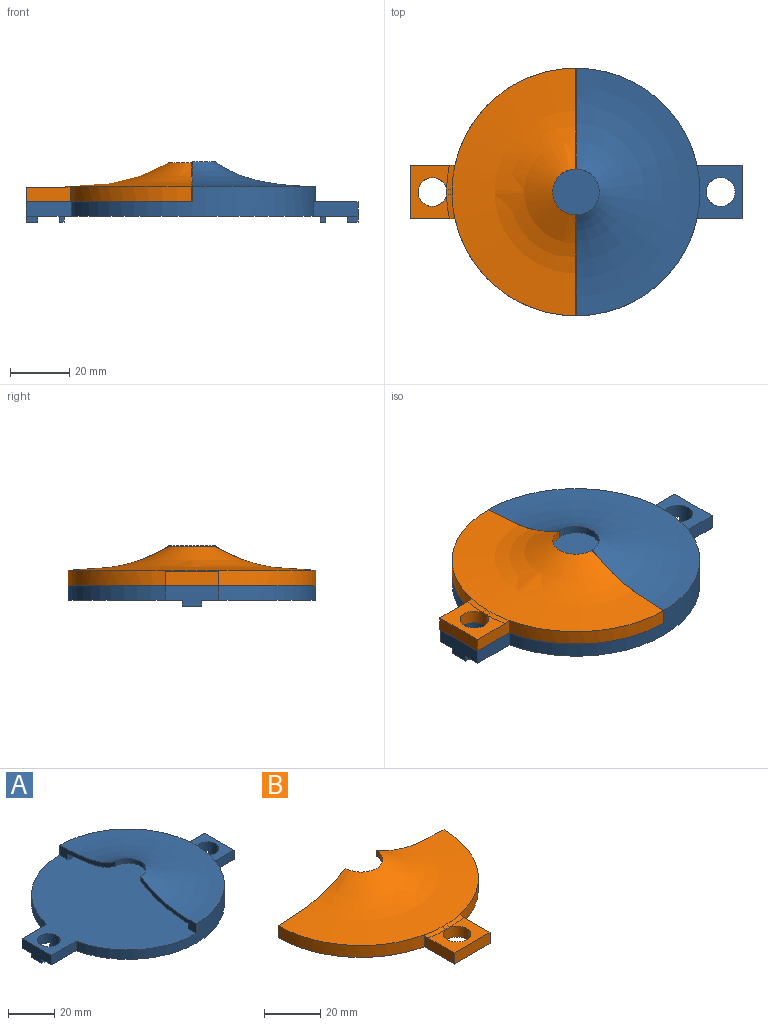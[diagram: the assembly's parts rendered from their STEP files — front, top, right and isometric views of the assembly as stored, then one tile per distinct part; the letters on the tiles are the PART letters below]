
ASSEMBLY  parts=2 mates=1
PART A: 32 faces, bbox 111.7x83.4x20.5 mm
  f0: plane 2x1.61mm, normal (0,1,0), area 3.2mm2, adj f2,f12,f23,f31
  f1: plane 2x1.61mm, normal (0,-1,0), area 3.2mm2, adj f2,f12,f23,f31
  f2: plane 6.48x1.61mm, normal (0,0,-1), area 4.9mm2, adj f0,f1,f23,f31
  f3: plane 2x1.86mm, normal (0,1,0), area 3.7mm2, adj f12,f28,f29,f30
  f4: plane 2x1.86mm, normal (0,-1,0), area 3.7mm2, adj f12,f28,f29,f30
  f5: plane 6.48x3.55mm, normal (0,0,-1), area 17.6mm2, adj f20,f26,f27,f30
  f6: cylinder r=41.7mm len=83.4mm, axis (0,0,1), area 1805.7mm2, adj f10,f11,f12,f13,f14,f15,f17,f18
  f7: cylinder r=7.75mm len=15.5mm, axis (0,0,1), area 60.9mm2, adj f8,f10,f13,f14
  f8: revolved ~73.4x36.7mm, area 2087.5mm2, adj f7,f9,f13,f14
  f9: cylinder r=36.7mm len=73.4mm, axis (0,0,1), area 334.4mm2, adj f8,f11,f13,f14
  f10: revolved ~83.4x41.7mm, area 2706.3mm2, adj f6,f7,f13,f14
  f11: plane 92.56x83.4mm, normal (0,0,1), area 5032.3mm2, adj f6,f9,f13,f14,f15,f16,f17,f31
  f12: plane 111.72x83.4mm, normal (0,0,-1), area 5785mm2, adj f0,f1,f3,f4,f6,f15,f16,f17
  f13: plane 33.95x13.46mm, normal (-1,0,0), area 93.5mm2, adj f6,f7,f8,f9,f10,f11
  f14: plane 33.95x13.46mm, normal (-1,0,0), area 93.5mm2, adj f6,f7,f8,f9,f10,f11
  f15: plane 15.14x5mm, normal (0,-1,0), area 75.7mm2, adj f6,f11,f12,f16
  f16: plane 17.94x7mm, normal (-1,0,0), area 102.6mm2, adj f11,f12,f15,f17,f22,f24,f25
  f17: plane 15.14x5mm, normal (0,1,0), area 75.7mm2, adj f6,f11,f12,f16
  f18: plane 15.14x5mm, normal (0,-1,0), area 75.7mm2, adj f6,f12,f20,f21
  f19: plane 15.14x5mm, normal (0,1,0), area 75.7mm2, adj f6,f12,f20,f21
  f20: plane 17.94x7mm, normal (1,0,0), area 102.6mm2, adj f5,f12,f18,f19,f21,f26,f27
  f21: plane 17.94x15.14mm, normal (0,0,1), area 185.2mm2, adj f6,f18,f19,f20,f30
  f22: plane 3.81x2mm, normal (0,1,0), area 7.6mm2, adj f12,f16,f25,f31
  f23: plane 6.48x2mm, normal (1,0,0), area 13mm2, adj f0,f1,f2,f12
  f24: plane 3.81x2mm, normal (0,-1,0), area 7.6mm2, adj f12,f16,f25,f31
  f25: plane 6.48x3.81mm, normal (0,0,-1), area 19.2mm2, adj f16,f22,f24,f31
  f26: plane 3.55x2mm, normal (0,1,0), area 7.1mm2, adj f5,f12,f20,f30
  f27: plane 3.55x2mm, normal (0,-1,0), area 7.1mm2, adj f5,f12,f20,f30
  f28: plane 6.48x2mm, normal (-1,0,0), area 13mm2, adj f3,f4,f12,f29
  f29: plane 6.48x1.86mm, normal (0,0,-1), area 6.6mm2, adj f3,f4,f28,f30
  f30: cylinder r=4.87mm len=9.75mm, axis (0,0,1), area 181.4mm2, adj f3,f4,f5,f12,f21,f26,f27,f29
  f31: cylinder r=4.87mm len=9.75mm, axis (0,0,1), area 181.4mm2, adj f0,f1,f2,f11,f12,f22,f24,f25
PART B: 21 faces, bbox 83.4x55.9x13.2 mm
  f0: cylinder r=41.7mm len=40.72mm, axis (0,0,-1), area 291mm2, adj f6,f7,f9,f12,f15,f17
  f1: cylinder r=36.7mm len=73.4mm, axis (0,0,-1), area 332.5mm2, adj f3,f4,f7,f8,f9,f15,f16,f17
  f2: cylinder r=41.7mm len=40.72mm, axis (0,0,-1), area 291mm2, adj f3,f6,f8,f11,f15,f16
  f3: plane 36.12x20.86mm, normal (0,0,-1), area 198mm2, adj f1,f2,f8,f16
  f4: revolved ~73.4x36.7mm, area 2084.2mm2, adj f1,f5,f8,f9
  f5: cylinder r=7.75mm len=15.5mm, axis (0,0,-1), area 60.9mm2, adj f4,f6,f8,f9
  f6: revolved ~83.4x41.7mm, area 2700.5mm2, adj f0,f2,f5,f8,f9,f18,f19,f20
  f7: plane 36.12x20.86mm, normal (0,0,-1), area 198mm2, adj f0,f1,f9,f17
  f8: plane 33.95x13.14mm, normal (0,1,0), area 97.8mm2, adj f1,f2,f3,f4,f5,f6
  f9: plane 33.95x13.14mm, normal (0,1,0), area 97.8mm2, adj f0,f1,f4,f5,f6,f7
  f10: plane 17.94x4.79mm, normal (0,-1,0), area 85.9mm2, adj f11,f12,f13,f15
  f11: plane 15.12x5.12mm, normal (1,0,0), area 72.6mm2, adj f2,f10,f13,f15,f20
  f12: plane 15.12x5.12mm, normal (-1,0,0), area 72.6mm2, adj f0,f10,f13,f15,f18
  f13: plane 17.95x13.28mm, normal (0,0,1), area 152.3mm2, adj f10,f11,f12,f14,f18,f20
  f14: cylinder r=4.87mm len=9.75mm, axis (0,0,1), area 146.6mm2, adj f13,f15,f19
  f15: plane 41.69x25.63mm, normal (0,0,-1), area 404.6mm2, adj f0,f1,f2,f10,f11,f12,f14,f16
  f16: plane 5.91x0.04mm, normal (-1,0,0), area 0.2mm2, adj f1,f2,f3,f15
  f17: plane 5.91x0.04mm, normal (1,0,0), area 0.2mm2, adj f0,f1,f7,f15
  f18: bspline ~8.41x2.77mm, area 14.9mm2, adj f6,f12,f13,f19
  f19: bspline ~1.97x1.81mm, area 3.4mm2, adj f6,f14,f18,f20
  f20: bspline ~20.56x3.41mm, area 14.9mm2, adj f6,f11,f13,f19
PLACE A t=(8.5,-10.57,-12.15)mm
PLACE B rot(axis=(0,0,-1),90deg) t=(8.36,-10.57,-8.53)mm
MATE cylindrical B.f14 <-> A.f31  axis (0,0,1) through (-39.91,-10.57,-2.33)mm
